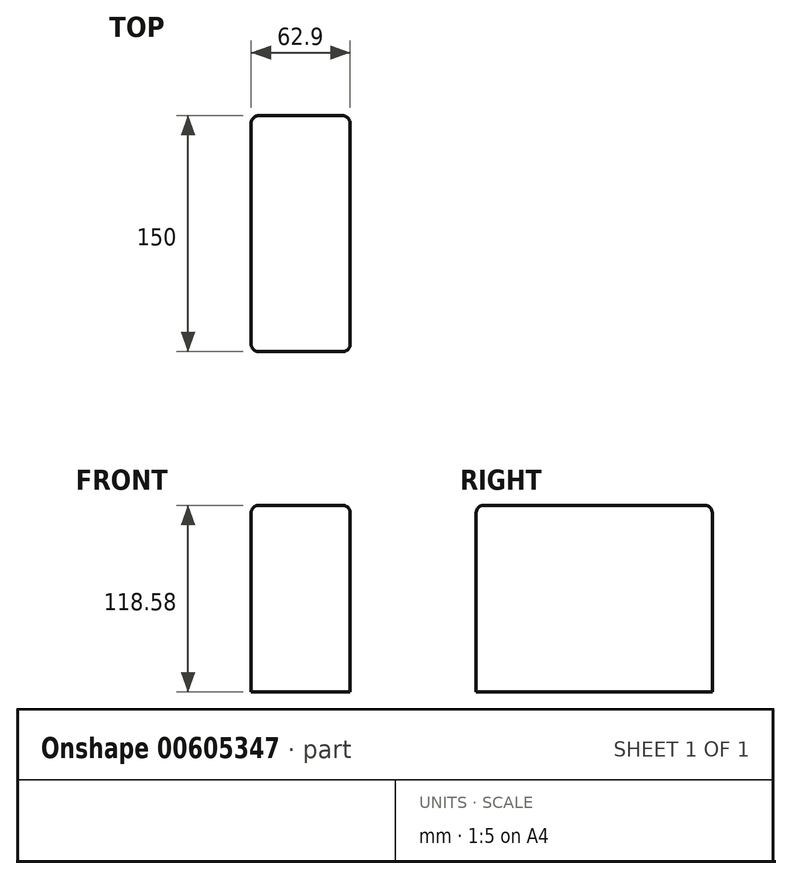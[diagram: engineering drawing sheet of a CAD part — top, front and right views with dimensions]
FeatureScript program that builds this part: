
annotation { "Feature Type Name" : "Feature", "Feature Type Description" : "" }
export const myFeature = defineFeature(function(context is Context, id is Id, definition is map)
    precondition{}
    {
        {
            var Q0;
            Q0=qCreatedBy(makeId("Front.planeOp"),FACE);
            var sketch = newSketch(context, id + "F0", { "sketchPlane" : qUnion([Q0])});
            skLineSegment(sketch, "E0.bottom", {"start": v(-31.45, 59.29) * mm, "end": v(31.45, 59.29) * mm});
            skLineSegment(sketch, "E0.top", {"start": v(-31.45, -59.29) * mm, "end": v(31.45, -59.29) * mm});
            skLineSegment(sketch, "E0.left", {"start": v(-31.45, 59.29) * mm, "end": v(-31.45, -59.29) * mm});
            skLineSegment(sketch, "E0.right", {"start": v(31.45, 59.29) * mm, "end": v(31.45, -59.29) * mm});
            skPoint(sketch, "E0.middle", {"position": v(0, 0) * mm});
            skSolve(sketch);
        }
        {
            var Q0;
            Q0=makeQuery(id+"F0.imprint","IMPRINT",FACE,{"disambiguationData":[TD([[makeQuery(id+"F0.imprint","IMPRINT",EDGE,{"derivedFrom":sQuery(id+"F0.wireOp",EDGE,"E0.bottom")}),-1.0]])]});
            extrude(context, id + "F1", {"entities" : qUnion([Q0]), "depth" : 150 * mm, "offsetDistance" : 25 * mm});
        }
        {
            var Q0;
            Q0=makeQuery(id+"F1.opExtrude","CAP_EDGE",EDGE,{"disambiguationData":[OSD([sQuery(id+"F0.wireOp",EDGE,"E0.bottom")])],"isStart":false});
            var Q1;
            Q1=makeQuery(id+"F1.opExtrude","CAP_EDGE",EDGE,{"disambiguationData":[OSD([sQuery(id+"F0.wireOp",EDGE,"E0.left")])],"isStart":false});
            var Q2;
            Q2=makeQuery(id+"F1.opExtrude","CAP_EDGE",EDGE,{"disambiguationData":[OSD([sQuery(id+"F0.wireOp",EDGE,"E0.right")])],"isStart":false});
            var Q3;
            Q3=makeQuery(id+"F1.opExtrude","SWEPT_EDGE",EDGE,{"disambiguationData":[OSD([sQuery(id+"F0.wireOp",EDGE,"E0.bottom"),sQuery(id+"F0.wireOp",EDGE,"E0.left")])]});
            var Q4;
            Q4=makeQuery(id+"F1.opExtrude","SWEPT_EDGE",EDGE,{"disambiguationData":[OSD([sQuery(id+"F0.wireOp",EDGE,"E0.bottom"),sQuery(id+"F0.wireOp",EDGE,"E0.right")])]});
            var Q5;
            Q5=makeQuery(id+"F1.opExtrude","CAP_EDGE",EDGE,{"disambiguationData":[OSD([sQuery(id+"F0.wireOp",EDGE,"E0.bottom")])],"isStart":true});
            var Q6;
            Q6=makeQuery(id+"F1.opExtrude","CAP_EDGE",EDGE,{"disambiguationData":[OSD([sQuery(id+"F0.wireOp",EDGE,"E0.left")])],"isStart":true});
            var Q7;
            Q7=makeQuery(id+"F1.opExtrude","CAP_EDGE",EDGE,{"disambiguationData":[OSD([sQuery(id+"F0.wireOp",EDGE,"E0.right")])],"isStart":true});
            fillet(context, id + "F2", {"entities" : qUnion([Q0, Q1, Q2, Q3, Q4, Q5, Q6, Q7]), "radius" : 5 * mm, "tangentPropagation" : true, "allowEdgeOverflow" : false});
        }
    });
